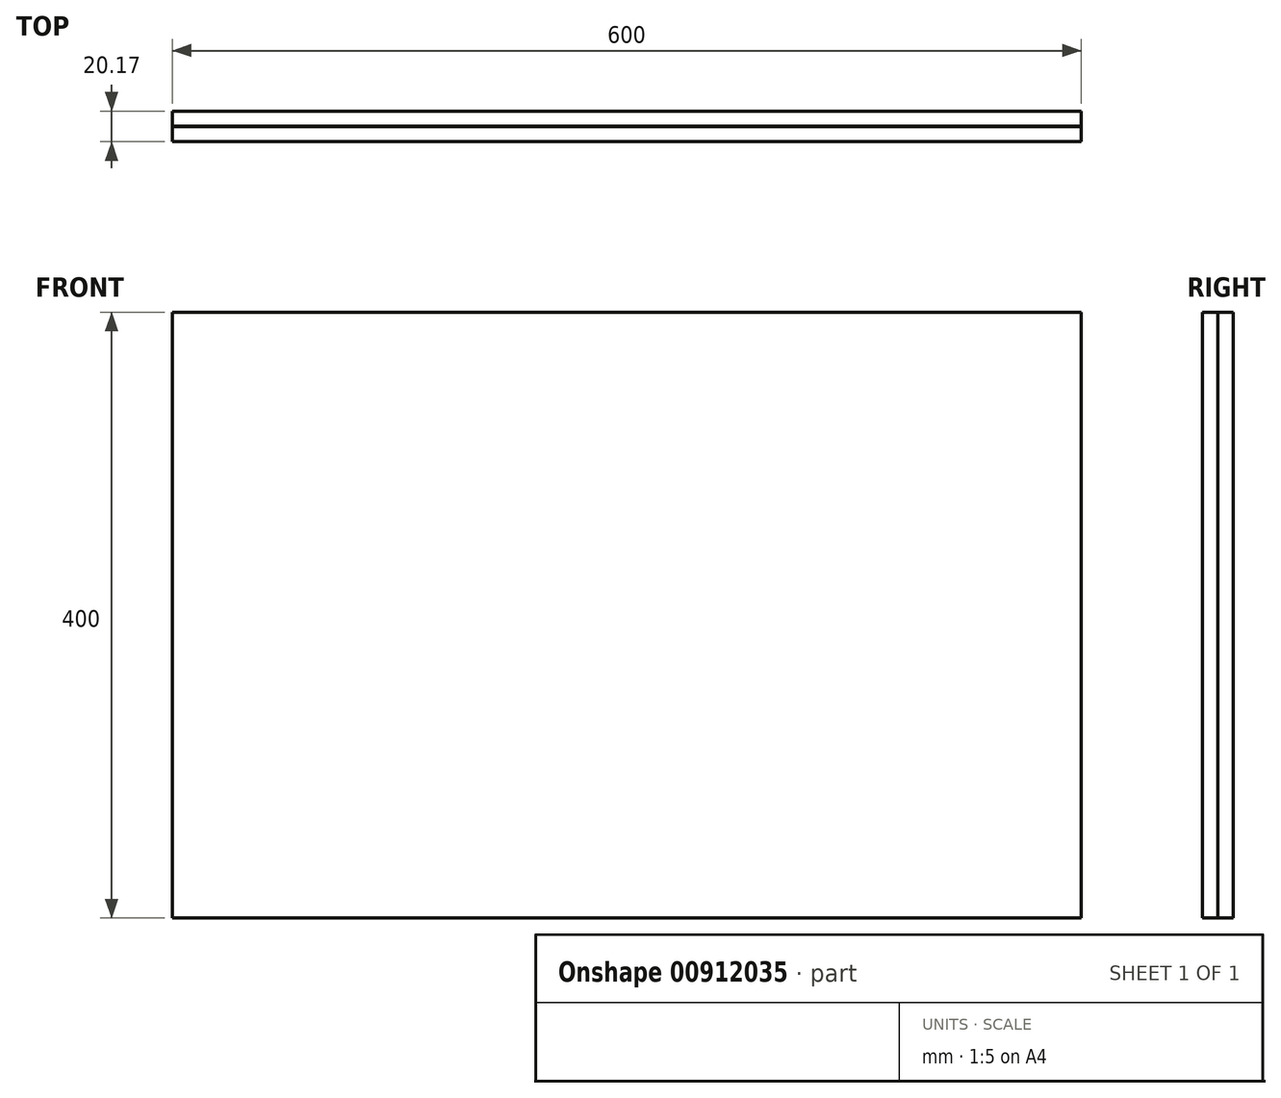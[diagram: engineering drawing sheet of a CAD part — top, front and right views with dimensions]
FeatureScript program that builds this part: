
annotation { "Feature Type Name" : "Feature", "Feature Type Description" : "" }
export const myFeature = defineFeature(function(context is Context, id is Id, definition is map)
    precondition{}
    {
        {
            var Q0;
            Q0=qCreatedBy(makeId("Right.planeOp"),FACE);
            var sketch = newSketch(context, id + "F0", { "sketchPlane" : qUnion([Q0])});
            skLineSegment(sketch, "E0.bottom", {"start": v(5, -200) * mm, "end": v(-5, -200) * mm});
            skLineSegment(sketch, "E0.top", {"start": v(5, 200) * mm, "end": v(-5, 200) * mm});
            skLineSegment(sketch, "E0.left", {"start": v(5, -200) * mm, "end": v(5, 200) * mm});
            skLineSegment(sketch, "E0.right", {"start": v(-5, -200) * mm, "end": v(-5, 200) * mm});
            skPoint(sketch, "E0.middle", {"position": v(0, 0) * mm});
            skLineSegment(sketch, "E1.bottom", {"start": v(15.17, -200) * mm, "end": v(5.17, -200) * mm});
            skLineSegment(sketch, "E1.top", {"start": v(15.17, 200) * mm, "end": v(5.17, 200) * mm});
            skLineSegment(sketch, "E1.left", {"start": v(15.17, -200) * mm, "end": v(15.17, 200) * mm});
            skLineSegment(sketch, "E1.right", {"start": v(5.17, -200) * mm, "end": v(5.17, 200) * mm});
            skPoint(sketch, "E1.middle", {"position": v(10.17, 0) * mm});
            skSolve(sketch);
        }
        {
            var Q0;
            Q0=makeQuery(id+"F0.imprint","IMPRINT",FACE,{"disambiguationData":[TD([[makeQuery(id+"F0.imprint","IMPRINT",EDGE,{"derivedFrom":sQuery(id+"F0.wireOp",EDGE,"E1.bottom")}),-1.0]])]});
            var Q1;
            Q1=makeQuery(id+"F0.imprint","IMPRINT",FACE,{"disambiguationData":[TD([[makeQuery(id+"F0.imprint","IMPRINT",EDGE,{"derivedFrom":sQuery(id+"F0.wireOp",EDGE,"E0.bottom")}),-1.0]])]});
            extrude(context, id + "F1", {"entities" : qUnion([Q0, Q1]), "depth" : 600 * mm, "offsetDistance" : 25 * mm});
        }
    });
